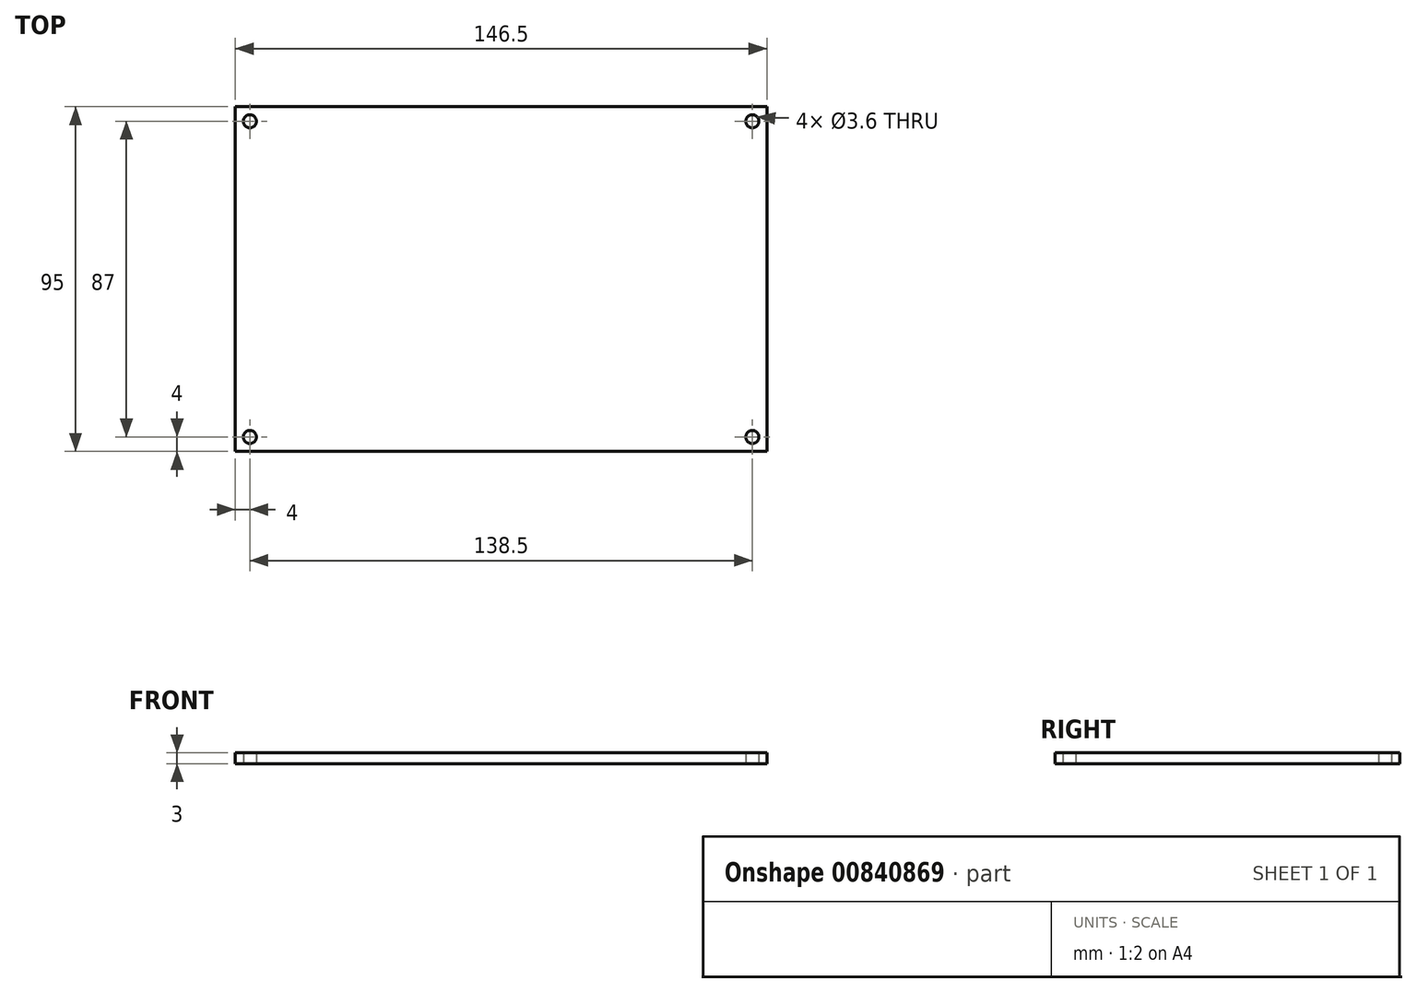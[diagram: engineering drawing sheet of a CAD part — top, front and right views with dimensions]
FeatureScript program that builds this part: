
annotation { "Feature Type Name" : "Feature", "Feature Type Description" : "" }
export const myFeature = defineFeature(function(context is Context, id is Id, definition is map)
    precondition{}
    {
        {
            var Q0;
            Q0=qCreatedBy(makeId("Top.planeOp"),FACE);
            var sketch = newSketch(context, id + "F0", { "sketchPlane" : qUnion([Q0])});
            skLineSegment(sketch, "E0.bottom", {"start": v(0, 0) * mm, "end": v(146.5, 0) * mm});
            skLineSegment(sketch, "E0.top", {"start": v(0, 95) * mm, "end": v(146.5, 95) * mm});
            skLineSegment(sketch, "E0.left", {"start": v(0, 0) * mm, "end": v(0, 95) * mm});
            skLineSegment(sketch, "E0.right", {"start": v(146.5, 0) * mm, "end": v(146.5, 95) * mm});
            skCircle(sketch, "E1", {"center": v(4, 91) * mm, "radius": 1.8 * mm});
            skLineSegment(sketch, "E2", {"start": v(0, 47.5) * mm, "end": v(146.5, 47.5) * mm, "construction": true});
            skLineSegment(sketch, "E3", {"start": v(73.25, 95) * mm, "end": v(73.25, 0) * mm, "construction": true});
            skCircle(sketch, "E4.MirrorC", {"center": v(4, 4) * mm, "radius": 1.8 * mm});
            skCircle(sketch, "E5.MirrorC", {"center": v(142.5, 91) * mm, "radius": 1.8 * mm});
            skCircle(sketch, "E6.MirrorC", {"center": v(142.5, 4) * mm, "radius": 1.8 * mm});
            skSolve(sketch);
        }
        {
            var Q0;
            Q0=qSketchRegion(id+"F0",true);
            extrude(context, id + "F1", {"entities" : qUnion([Q0]), "depth" : 3 * mm, "offsetDistance" : 25 * mm});
        }
    });
